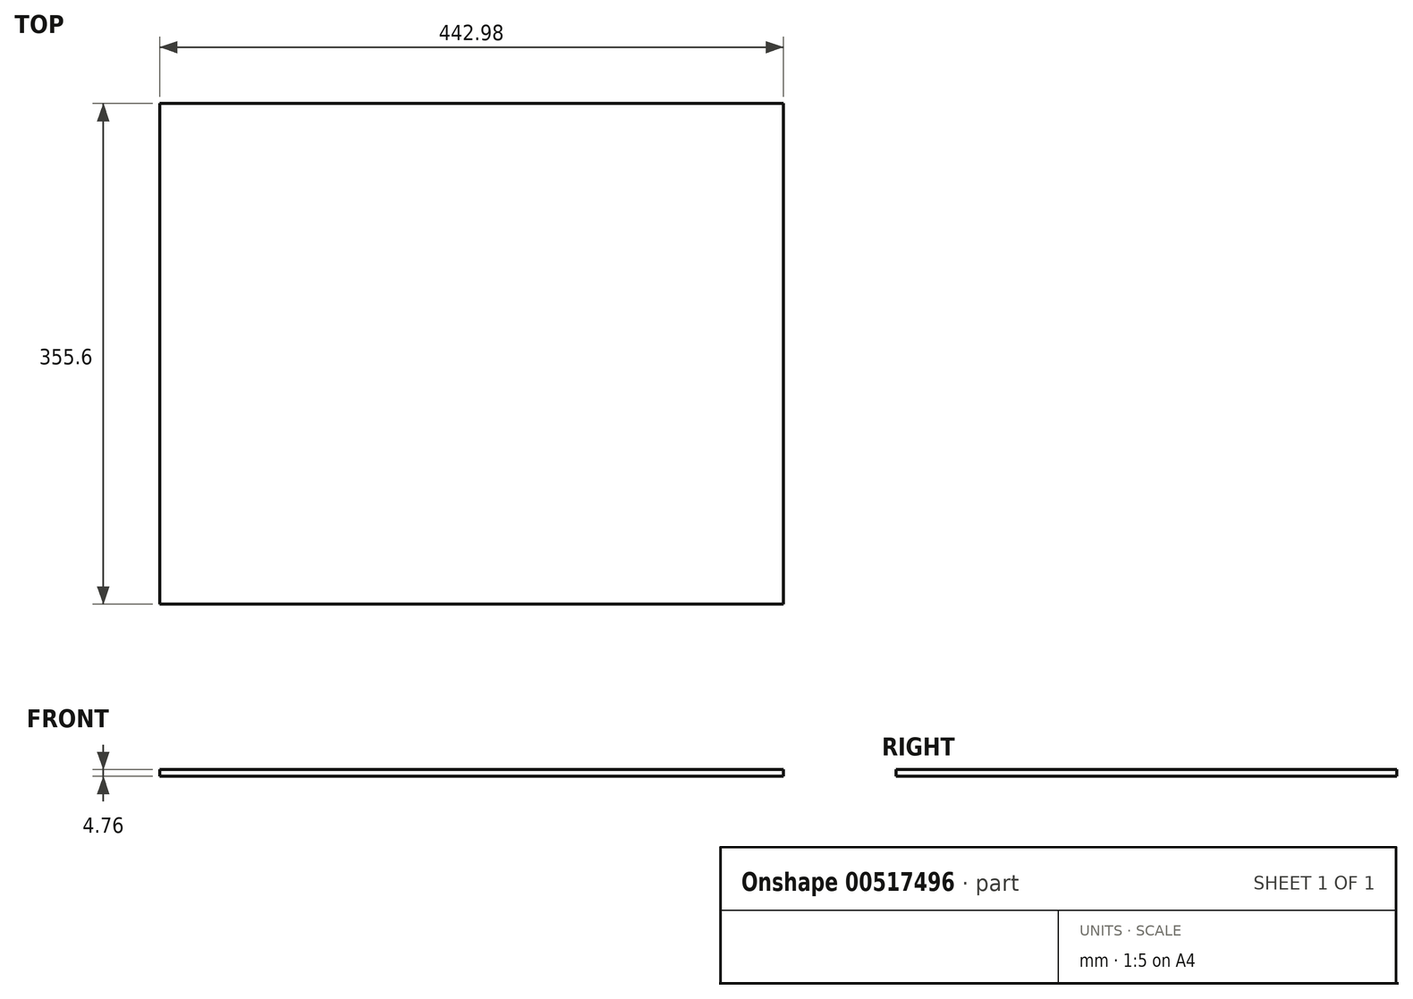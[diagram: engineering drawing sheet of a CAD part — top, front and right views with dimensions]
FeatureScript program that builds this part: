
annotation { "Feature Type Name" : "Feature", "Feature Type Description" : "" }
export const myFeature = defineFeature(function(context is Context, id is Id, definition is map)
    precondition{}
    {
        {
            var Q0;
            Q0=qCreatedBy(makeId("Top.planeOp"),FACE);
            var sketch = newSketch(context, id + "F0", { "sketchPlane" : qUnion([Q0])});
            skLineSegment(sketch, "E0.bottom", {"start": v(221.49, -177.8) * mm, "end": v(-221.49, -177.8) * mm});
            skLineSegment(sketch, "E0.top", {"start": v(221.49, 177.8) * mm, "end": v(-221.49, 177.8) * mm});
            skLineSegment(sketch, "E0.left", {"start": v(221.49, -177.8) * mm, "end": v(221.49, 177.8) * mm});
            skLineSegment(sketch, "E0.right", {"start": v(-221.49, -177.8) * mm, "end": v(-221.49, 177.8) * mm});
            skPoint(sketch, "E0.middle", {"position": v(0, 0) * mm});
            skSolve(sketch);
        }
        {
            var Q0;
            Q0=makeQuery(id+"F0.imprint","IMPRINT",FACE,{"disambiguationData":[TD([[makeQuery(id+"F0.imprint","IMPRINT",EDGE,{"derivedFrom":sQuery(id+"F0.wireOp",EDGE,"E0.bottom")}),-1.0]])]});
            extrude(context, id + "F1", {"entities" : qUnion([Q0]), "depth" : 4.76 * mm, "offsetDistance" : 25.4 * mm});
        }
    });
